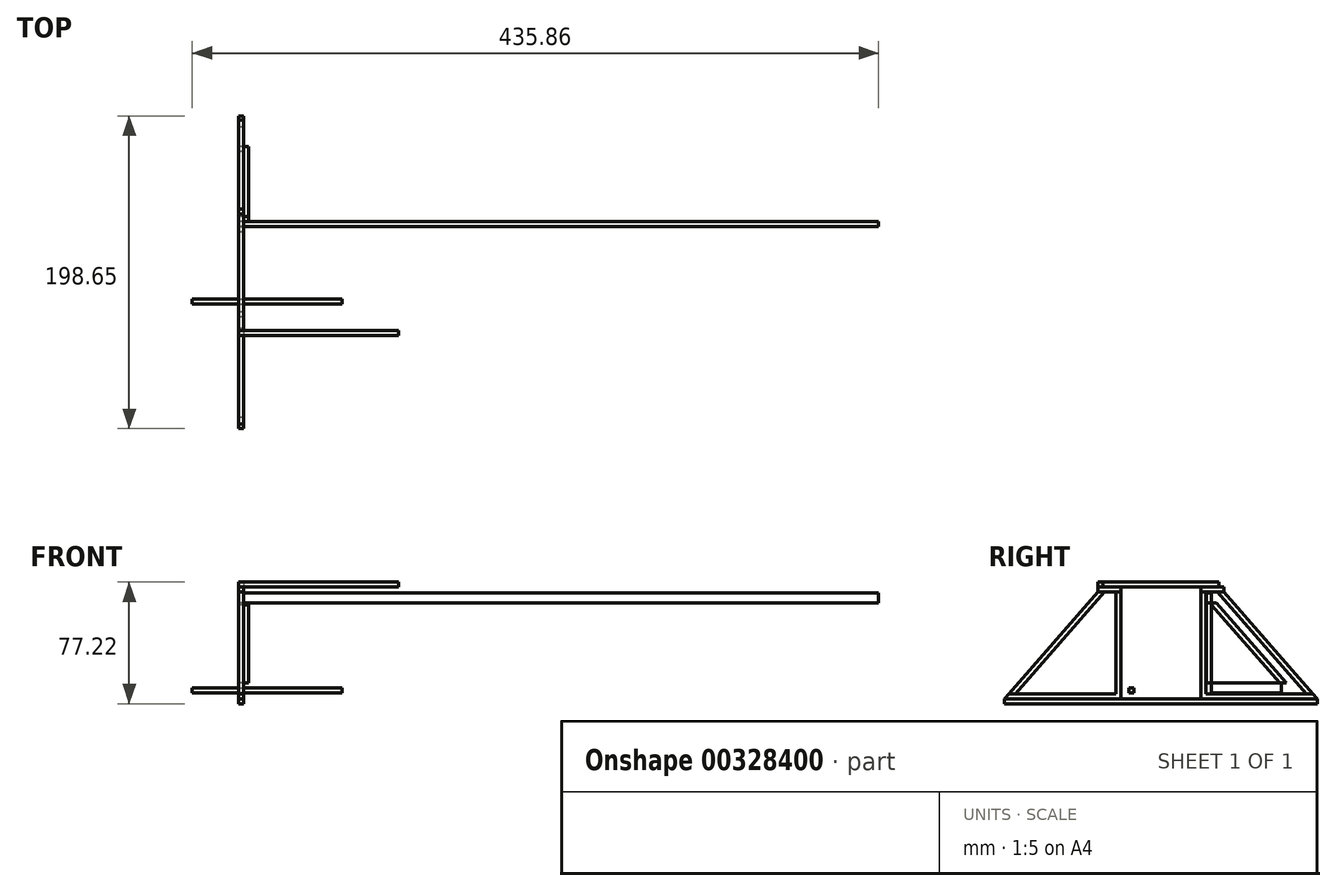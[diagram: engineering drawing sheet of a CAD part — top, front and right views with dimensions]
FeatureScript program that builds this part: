
annotation { "Feature Type Name" : "Feature", "Feature Type Description" : "" }
export const myFeature = defineFeature(function(context is Context, id is Id, definition is map)
    precondition{}
    {
        {
            var Q0;
            Q0=qCreatedBy(makeId("Right.planeOp"),FACE);
            var sketch = newSketch(context, id + "F0", { "sketchPlane" : qUnion([Q0])});
            skLineSegment(sketch, "E0", {"start": v(0, 0) * mm, "end": v(0, 6.35) * mm});
            skLineSegment(sketch, "E1", {"start": v(0, 6.35) * mm, "end": v(3.17, 6.35) * mm});
            skLineSegment(sketch, "E2", {"start": v(3.18, 6.35) * mm, "end": v(3.18, 0) * mm});
            skLineSegment(sketch, "E3", {"start": v(3.18, 0) * mm, "end": v(0, 0) * mm});
            skLineSegment(sketch, "E4", {"start": v(3.18, 6.35) * mm, "end": v(47.63, 6.35) * mm});
            skLineSegment(sketch, "E5", {"start": v(47.63, 6.35) * mm, "end": v(47.63, 0) * mm});
            skLineSegment(sketch, "E6", {"start": v(47.63, 0) * mm, "end": v(3.18, 0) * mm});
            skLineSegment(sketch, "E7", {"start": v(47.63, 6.35) * mm, "end": v(50.8, 6.35) * mm});
            skLineSegment(sketch, "E8", {"start": v(50.8, 6.35) * mm, "end": v(50.8, 0) * mm});
            skLineSegment(sketch, "E9", {"start": v(50.8, 0) * mm, "end": v(47.63, 0) * mm});
            skLineSegment(sketch, "E10", {"start": v(3.17, 63.5) * mm, "end": v(3.17, 57.15) * mm});
            skLineSegment(sketch, "E11", {"start": v(3.17, 57.15) * mm, "end": v(6.35, 57.15) * mm});
            skLineSegment(sketch, "E12", {"start": v(6.35, 57.15) * mm, "end": v(6.35, 63.5) * mm});
            skLineSegment(sketch, "E13", {"start": v(6.35, 63.5) * mm, "end": v(3.17, 63.5) * mm});
            skLineSegment(sketch, "E14", {"start": v(0, 63.5) * mm, "end": v(0, 57.15) * mm});
            skLineSegment(sketch, "E15", {"start": v(0, 57.15) * mm, "end": v(3.17, 57.15) * mm});
            skLineSegment(sketch, "E16", {"start": v(0, 63.5) * mm, "end": v(3.17, 63.5) * mm});
            skLineSegment(sketch, "E17", {"start": v(0, 6.35) * mm, "end": v(0, 57.15) * mm});
            skLineSegment(sketch, "E18", {"start": v(50.8, 6.35) * mm, "end": v(6.35, 57.15) * mm});
            skLineSegment(sketch, "E19", {"start": v(3.18, 6.35) * mm, "end": v(3.17, 55.96) * mm});
            skLineSegment(sketch, "E20", {"start": v(3.17, 55.96) * mm, "end": v(46.58, 6.35) * mm});
            skPoint(sketch, "E21.orphan", {"position": v(3.17, 51.01) * mm});
            skLineSegment(sketch, "E22", {"start": v(3.17, 55.96) * mm, "end": v(3.17, 57.15) * mm});
            skSolve(sketch);
        }
        {
            var Q0;
            Q0=makeQuery(id+"F0.imprint","IMPRINT",FACE,{"disambiguationData":[TD([[makeQuery(id+"F0.imprint","IMPRINT",EDGE,{"derivedFrom":sQuery(id+"F0.wireOp",EDGE,"E1")}),1.0]])]});
            extrude(context, id + "F1", {"entities" : qUnion([Q0]), "depth" : 3.17 * mm});
        }
        {
            var Q0;
            Q0=makeQuery(id+"F0.imprint","IMPRINT",FACE,{"disambiguationData":[TD([[makeQuery(id+"F0.imprint","IMPRINT",EDGE,{"derivedFrom":sQuery(id+"F0.wireOp",EDGE,"E10")}),-1.0]])]});
            extrude(context, id + "F2", {"entities" : qUnion([Q0]), "depth" : 406.4 * mm});
        }
        {
            var Q0;
            {var subQ3=sQuery(id+"F0.wireOp",EDGE,"E2");Q0=makeQuery(id+"F0.imprint","IMPRINT",FACE,{"disambiguationData":[TD([[makeQuery(id+"F0.imprint","IMPRINT",EDGE,{"derivedFrom":subQ3}),1.0]])]});}
            extrude(context, id + "F3", {"entities" : qUnion([Q0]), "depth" : 3.17 * mm});
        }
        {
            var Q0;
            {var subQ0=sQuery(id+"F0.wireOp",EDGE,"E7");Q0=makeQuery(id+"F0.imprint","IMPRINT",FACE,{"disambiguationData":[TD([[makeQuery(id+"F0.imprint","IMPRINT",EDGE,{"derivedFrom":subQ0}),1.0]])]});}
            extrude(context, id + "F4", {"entities" : qUnion([Q0]), "depth" : 6.35 * mm, "offsetDistance" : 25.4 * mm});
        }
        {
            var Q0;
            {var subQ3=sQuery(id+"F0.wireOp",EDGE,"E2");Q0=makeQuery(id+"F0.imprint","IMPRINT",FACE,{"disambiguationData":[TD([[makeQuery(id+"F0.imprint","IMPRINT",EDGE,{"derivedFrom":subQ3}),1.0]])]});}
            var sketch = newSketch(context, id + "F5", { "sketchPlane" : qUnion([Q0])});
            skLineSegment(sketch, "E23", {"start": v(-0.5, 64) * mm, "end": v(-0.5, -0.5) * mm});
            skLineSegment(sketch, "E24", {"start": v(-0.5, -0.5) * mm, "end": v(63.24, -0.5) * mm});
            skLineSegment(sketch, "E25", {"start": v(63.24, -0.5) * mm, "end": v(6.8, 64) * mm});
            skLineSegment(sketch, "E26.0", {"start": v(-3.68, 64) * mm, "end": v(-3.68, -3.68) * mm});
            skLineSegment(sketch, "E26.1", {"start": v(70.24, -3.68) * mm, "end": v(11.01, 64) * mm});
            skLineSegment(sketch, "E26.2", {"start": v(-3.68, -3.68) * mm, "end": v(70.24, -3.68) * mm});
            skLineSegment(sketch, "E27", {"start": v(63.24, -0.5) * mm, "end": v(67.46, -0.5) * mm});
            skLineSegment(sketch, "E28", {"start": v(-3.68, 64) * mm, "end": v(11.01, 64) * mm});
            skLineSegment(sketch, "E29.0", {"start": v(-3.68, 67.18) * mm, "end": v(11.01, 67.18) * mm});
            skLineSegment(sketch, "E30", {"start": v(-3.68, 64) * mm, "end": v(-3.68, 67.18) * mm});
            skLineSegment(sketch, "E31", {"start": v(11.01, 64) * mm, "end": v(11.01, 67.18) * mm});
            skLineSegment(sketch, "E32", {"start": v(11.01, 67.18) * mm, "end": v(-69.18, 67.18) * mm});
            skLineSegment(sketch, "E33.0", {"start": v(11.01, 70.36) * mm, "end": v(-69.18, 70.36) * mm});
            skLineSegment(sketch, "E34", {"start": v(11.01, 67.18) * mm, "end": v(11.01, 70.36) * mm});
            skLineSegment(sketch, "E35", {"start": v(-3.68, 67.18) * mm, "end": v(-3.68, 70.36) * mm, "construction": true});
            skLineSegment(sketch, "E36", {"start": v(-69.18, 67.18) * mm, "end": v(-69.18, 70.36) * mm});
            skLineSegment(sketch, "E37", {"start": v(-49.25, 70.36) * mm, "end": v(-49.25, 67.18) * mm, "construction": true});
            skLineSegment(sketch, "E38", {"start": v(70.24, -3.68) * mm, "end": v(-128.4, -3.68) * mm});
            skLineSegment(sketch, "E39.0", {"start": v(70.24, -6.86) * mm, "end": v(-128.4, -6.86) * mm});
            skLineSegment(sketch, "E40", {"start": v(70.24, -6.86) * mm, "end": v(70.24, -3.68) * mm});
            skLineSegment(sketch, "E41", {"start": v(-128.4, -6.86) * mm, "end": v(-128.4, -3.68) * mm});
            skLineSegment(sketch, "E42", {"start": v(-29.08, 70.36) * mm, "end": v(-29.08, -6.86) * mm, "construction": true});
            skLineSegment(sketch, "E43.MirrorCS", {"start": v(-54.48, 64) * mm, "end": v(-54.48, 67.18) * mm});
            skLineSegment(sketch, "E44.MirrorCS", {"start": v(-69.18, 64) * mm, "end": v(-69.18, 67.18) * mm});
            skLineSegment(sketch, "E45.MirrorCS", {"start": v(-121.41, -0.5) * mm, "end": v(-125.63, -0.5) * mm});
            skLineSegment(sketch, "E46.MirrorCS", {"start": v(-54.48, 64) * mm, "end": v(-69.18, 64) * mm});
            skLineSegment(sketch, "E47.MirrorCS", {"start": v(-57.66, 64) * mm, "end": v(-57.66, -0.5) * mm});
            skLineSegment(sketch, "E48.MirrorCS", {"start": v(-57.66, -0.5) * mm, "end": v(-121.41, -0.5) * mm});
            skLineSegment(sketch, "E49.MirrorCS", {"start": v(-121.41, -0.5) * mm, "end": v(-64.96, 64) * mm});
            skLineSegment(sketch, "E50.MirrorCS", {"start": v(-54.48, 64) * mm, "end": v(-54.48, -3.68) * mm});
            skLineSegment(sketch, "E51.MirrorCS", {"start": v(-128.4, -3.68) * mm, "end": v(-69.18, 64) * mm});
            skLineSegment(sketch, "E52", {"start": v(-66, 70.36) * mm, "end": v(-66, 67.18) * mm});
            skLineSegment(sketch, "E53", {"start": v(7.84, 70.36) * mm, "end": v(7.84, 67.18) * mm});
            skSolve(sketch);
        }
        {
            var Q0;
            {var subQ0=sQuery(id+"F5.wireOp",EDGE,"E30");Q0=makeQuery(id+"F5.imprint","IMPRINT",FACE,{"disambiguationData":[TD([[makeQuery(id+"F5.imprint","IMPRINT",EDGE,{"derivedFrom":subQ0}),-1.0]])]});}
            var Q1;
            {var subQ1=sQuery(id+"F5.wireOp",EDGE,"E43.MirrorCS");Q1=makeQuery(id+"F5.imprint","IMPRINT",FACE,{"disambiguationData":[TD([[makeQuery(id+"F5.imprint","IMPRINT",EDGE,{"derivedFrom":subQ1}),1.0]])]});}
            extrude(context, id + "F6", {"entities" : qUnion([Q0, Q1]), "depth" : 3.17 * mm});
        }
        {
            var Q0;
            Q0=makeQuery(id+"F5.imprint","IMPRINT",FACE,{"disambiguationData":[TD([[makeQuery(id+"F5.imprint","IMPRINT",EDGE,{"derivedFrom":sQuery(id+"F5.wireOp",EDGE,"E39.0")}),-1.0]])]});
            extrude(context, id + "F7", {"entities" : qUnion([Q0]), "depth" : 3.17 * mm});
        }
        {
            var Q0;
            {var subQ5=sQuery(id+"F5.wireOp",EDGE,"E23");Q0=makeQuery(id+"F5.imprint","IMPRINT",FACE,{"disambiguationData":[TD([[makeQuery(id+"F5.imprint","IMPRINT",EDGE,{"derivedFrom":subQ5}),-1.0]])]});}
            var Q1;
            {var subQ3=sQuery(id+"F5.wireOp",EDGE,"E45.MirrorCS");Q1=makeQuery(id+"F5.imprint","IMPRINT",FACE,{"disambiguationData":[TD([[makeQuery(id+"F5.imprint","IMPRINT",EDGE,{"derivedFrom":subQ3}),1.0]])]});}
            extrude(context, id + "F8", {"entities" : qUnion([Q0, Q1]), "depth" : 3.17 * mm});
        }
        {
            var Q0;
            {var subQ0=sQuery(id+"F5.wireOp",EDGE,"E25");Q0=makeQuery(id+"F5.imprint","IMPRINT",FACE,{"disambiguationData":[TD([[makeQuery(id+"F5.imprint","IMPRINT",EDGE,{"derivedFrom":subQ0}),-1.0]])]});}
            var Q1;
            {var subQ0=sQuery(id+"F5.wireOp",EDGE,"E45.MirrorCS");Q1=makeQuery(id+"F5.imprint","IMPRINT",FACE,{"disambiguationData":[TD([[makeQuery(id+"F5.imprint","IMPRINT",EDGE,{"derivedFrom":subQ0}),-1.0]])]});}
            extrude(context, id + "F9", {"entities" : qUnion([Q0, Q1]), "depth" : 3.17 * mm});
        }
        {
            var Q0;
            {var subQ2=sQuery(id+"F5.wireOp",EDGE,"E52");Q0=makeQuery(id+"F5.imprint","IMPRINT",FACE,{"disambiguationData":[TD([[makeQuery(id+"F5.imprint","IMPRINT",EDGE,{"derivedFrom":subQ2}),1.0]])]});}
            extrude(context, id + "F10", {"entities" : qUnion([Q0]), "depth" : 3.17 * mm});
        }
        {
            var Q0;
            {var subQ0=sQuery(id+"F5.wireOp",EDGE,"E36");Q0=makeQuery(id+"F5.imprint","IMPRINT",FACE,{"disambiguationData":[TD([[makeQuery(id+"F5.imprint","IMPRINT",EDGE,{"derivedFrom":subQ0}),-1.0]])]});}
            extrude(context, id + "F11", {"entities" : qUnion([Q0]), "depth" : 101.6 * mm});
        }
        {
            var Q0;
            Q0=qCreatedBy(makeId("Top.planeOp"),FACE);
            var sketch = newSketch(context, id + "F12", { "sketchPlane" : qUnion([Q0])});
            skLineSegment(sketch, "E54.bottom", {"start": v(-29.46, -46.14) * mm, "end": v(65.8, -46.14) * mm});
            skLineSegment(sketch, "E54.top", {"start": v(-29.46, -49.32) * mm, "end": v(65.8, -49.32) * mm});
            skLineSegment(sketch, "E54.left", {"start": v(-29.46, -46.14) * mm, "end": v(-29.46, -49.32) * mm});
            skLineSegment(sketch, "E54.right", {"start": v(65.8, -46.14) * mm, "end": v(65.8, -49.32) * mm});
            skSolve(sketch);
        }
        {
            var Q0;
            Q0 = qSketchRegion(id + "F12", true);
            extrude(context, id + "F13", {"entities" : qUnion([Q0]), "depth" : 3.17 * mm});
        }
    });
